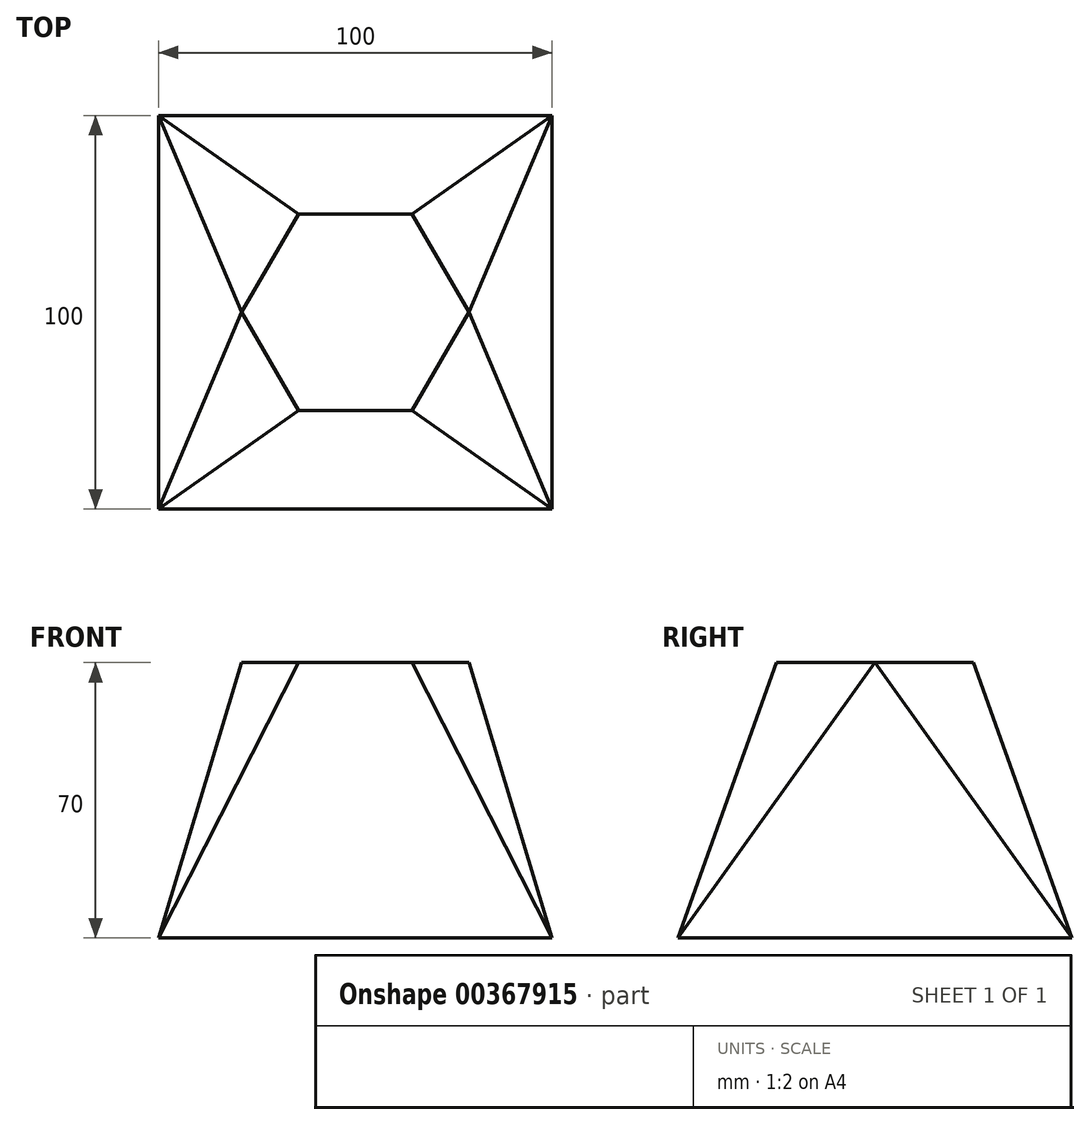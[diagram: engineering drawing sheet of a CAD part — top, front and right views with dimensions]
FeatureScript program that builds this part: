
annotation { "Feature Type Name" : "Feature", "Feature Type Description" : "" }
export const myFeature = defineFeature(function(context is Context, id is Id, definition is map)
    precondition{}
    {
        {
            var Q0;
            Q0=qCreatedBy(makeId("Top.planeOp"),FACE);
            cPlane(context, id + "F0", {"entities" : qUnion([Q0]), "cplaneType" : CPlaneType.OFFSET, "offset" : 70 * mm, "width" : 150 * mm, "height" : 150 * mm});
        }
        {
            var Q0;
            Q0=qCreatedBy(id+"F0.planeOp",FACE);
            var sketch = newSketch(context, id + "F1", { "sketchPlane" : qUnion([Q0])});
            skCircle(sketch, "E0.cCircle", {"center": v(0, 0) * mm, "radius": 25 * mm, "construction": true});
            skLineSegment(sketch, "E0.0", {"start": v(28.87, 0) * mm, "end": v(14.43, -25) * mm});
            skLineSegment(sketch, "E0.1", {"start": v(14.43, -25) * mm, "end": v(-14.43, -25) * mm});
            skLineSegment(sketch, "E0.2", {"start": v(-14.43, -25) * mm, "end": v(-28.87, 0) * mm});
            skLineSegment(sketch, "E0.3", {"start": v(-28.87, 0) * mm, "end": v(-14.43, 25) * mm});
            skLineSegment(sketch, "E0.4", {"start": v(-14.43, 25) * mm, "end": v(14.43, 25) * mm});
            skLineSegment(sketch, "E0.5", {"start": v(14.43, 25) * mm, "end": v(28.87, 0) * mm});
            skPoint(sketch, "E0.0.midPoint", {"position": v(21.65, -12.5) * mm});
            skLineSegment(sketch, "E1", {"start": v(-14.43, 25) * mm, "end": v(-14.43, -25) * mm});
            skLineSegment(sketch, "E2", {"start": v(14.43, 25) * mm, "end": v(14.43, -25) * mm});
            skSolve(sketch);
        }
        {
            var Q0;
            Q0=qCreatedBy(makeId("Top.planeOp"),FACE);
            var sketch = newSketch(context, id + "F2", { "sketchPlane" : qUnion([Q0])});
            skLineSegment(sketch, "E3.bottom", {"start": v(-50, 50) * mm, "end": v(50, 50) * mm});
            skLineSegment(sketch, "E3.top", {"start": v(-50, -50) * mm, "end": v(50, -50) * mm});
            skLineSegment(sketch, "E3.left", {"start": v(-50, 50) * mm, "end": v(-50, -50) * mm});
            skLineSegment(sketch, "E3.right", {"start": v(50, 50) * mm, "end": v(50, -50) * mm});
            skLineSegment(sketch, "E4", {"start": v(0, -50) * mm, "end": v(0, 50) * mm, "construction": true});
            skSolve(sketch);
        }
        {
            var Q0;
            Q0=makeQuery(id+"F1.imprint","IMPRINT",FACE,{"disambiguationData":[TD([[makeQuery(id+"F1.imprint","IMPRINT",EDGE,{"derivedFrom":sQuery(id+"F1.wireOp",EDGE,"E0.1")}),-1.0]])]});
            var Q1;
            Q1=makeQuery(id+"F2.imprint","IMPRINT",FACE,{"disambiguationData":[TD([[makeQuery(id+"F2.imprint","IMPRINT",EDGE,{"derivedFrom":sQuery(id+"F2.wireOp",EDGE,"E3.bottom")}),-1.0]])]});
            loft(context, id + "F3", {"sheetProfilesArray" : [{ "sheetProfileEntities" : qUnion([Q0]) }, { "sheetProfileEntities" : qUnion([Q1]) }]});
        }
        {
            var Q1;
            Q1=makeQuery(id+"F1.imprint","IMPRINT",FACE,{"disambiguationData":[TD([[makeQuery(id+"F1.imprint","IMPRINT",EDGE,{"derivedFrom":sQuery(id+"F1.wireOp",EDGE,"E0.2")}),-1.0]])]});
            var Q2;
            Q2=sQuery(id+"F2.wireOp",VERTEX,"E3.left.end");
            loft(context, id + "F4", {"operationType" : NewBodyOperationType.ADD, "sheetProfilesArray" : [{ "sheetProfileEntities" : qUnion([Q1]) }, { "sheetProfileEntities" : qUnion([Q2]) }]});
        }
        {
            var Q1;
            Q1=makeQuery(id+"F1.imprint","IMPRINT",FACE,{"disambiguationData":[TD([[makeQuery(id+"F1.imprint","IMPRINT",EDGE,{"derivedFrom":sQuery(id+"F1.wireOp",EDGE,"E0.2")}),-1.0]])]});
            var Q2;
            Q2=sQuery(id+"F2.wireOp",VERTEX,"E3.left.start");
            loft(context, id + "F5", {"operationType" : NewBodyOperationType.ADD, "sheetProfilesArray" : [{ "sheetProfileEntities" : qUnion([Q1]) }, { "sheetProfileEntities" : qUnion([Q2]) }]});
        }
        {
            var Q1;
            Q1=makeQuery(id+"F5.opLoft","SWEPT_FACE",FACE,{"disambiguationData":[OSD([sQuery(id+"F1.wireOp",EDGE,"E0.1"),sQuery(id+"F1.wireOp",EDGE,"E0.2"),sQuery(id+"F1.wireOp",EDGE,"E0.3"),sQuery(id+"F1.wireOp",EDGE,"E1")])]});
            var Q2;
            Q2=makeQuery(id+"F4.opLoft","SWEPT_FACE",FACE,{"disambiguationData":[OSD([sQuery(id+"F1.wireOp",EDGE,"E0.2"),sQuery(id+"F1.wireOp",EDGE,"E0.3"),sQuery(id+"F1.wireOp",EDGE,"E0.4"),sQuery(id+"F1.wireOp",EDGE,"E1")])]});
            var Q3;
            Q3=sQuery(id+"F2.wireOp",VERTEX,"E3.bottom.start");
            var Q4;
            Q4=sQuery(id+"F2.wireOp",VERTEX,"E3.left.end");
            loft(context, id + "F6", {"operationType" : NewBodyOperationType.ADD, "sheetProfilesArray" : [{ "sheetProfileEntities" : qUnion([Q1]) }, { "sheetProfileEntities" : qUnion([Q2]) }], "matchConnections" : true, "connections" : [{ "connectionEntities" : qUnion([Q3, Q4]), "connectionEdgeQueries" : qUnion([]), "connectionEdgeParameters" : [] }]});
        }
        {
            var Q1;
            Q1=makeQuery(id+"F1.imprint","IMPRINT",FACE,{"disambiguationData":[TD([[makeQuery(id+"F1.imprint","IMPRINT",EDGE,{"derivedFrom":sQuery(id+"F1.wireOp",EDGE,"E0.0")}),-1.0]])]});
            var Q2;
            Q2=sQuery(id+"F2.wireOp",VERTEX,"E3.right.start");
            loft(context, id + "F7", {"operationType" : NewBodyOperationType.ADD, "sheetProfilesArray" : [{ "sheetProfileEntities" : qUnion([Q1]) }, { "sheetProfileEntities" : qUnion([Q2]) }]});
        }
        {
            var Q1;
            Q1=makeQuery(id+"F1.imprint","IMPRINT",FACE,{"disambiguationData":[TD([[makeQuery(id+"F1.imprint","IMPRINT",EDGE,{"derivedFrom":sQuery(id+"F1.wireOp",EDGE,"E0.0")}),-1.0]])]});
            var Q2;
            Q2=sQuery(id+"F2.wireOp",VERTEX,"E3.right.end");
            loft(context, id + "F8", {"operationType" : NewBodyOperationType.ADD, "sheetProfilesArray" : [{ "sheetProfileEntities" : qUnion([Q1]) }, { "sheetProfileEntities" : qUnion([Q2]) }]});
        }
        {
            var Q1;
            Q1=makeQuery(id+"F8.opLoft","SWEPT_FACE",FACE,{"disambiguationData":[OSD([sQuery(id+"F1.wireOp",EDGE,"E0.0"),sQuery(id+"F1.wireOp",EDGE,"E0.4"),sQuery(id+"F1.wireOp",EDGE,"E0.5"),sQuery(id+"F1.wireOp",EDGE,"E2")])]});
            var Q2;
            Q2=makeQuery(id+"F7.opLoft","SWEPT_FACE",FACE,{"disambiguationData":[OSD([sQuery(id+"F1.wireOp",EDGE,"E0.0"),sQuery(id+"F1.wireOp",EDGE,"E0.1"),sQuery(id+"F1.wireOp",EDGE,"E0.5"),sQuery(id+"F1.wireOp",EDGE,"E2")])]});
            var Q3;
            Q3=sQuery(id+"F2.wireOp",VERTEX,"E3.right.end");
            var Q4;
            Q4=sQuery(id+"F2.wireOp",VERTEX,"E3.right.start");
            loft(context, id + "F9", {"operationType" : NewBodyOperationType.ADD, "sheetProfilesArray" : [{ "sheetProfileEntities" : qUnion([Q1]) }, { "sheetProfileEntities" : qUnion([Q2]) }], "matchConnections" : true, "connections" : [{ "connectionEntities" : qUnion([Q3, Q4]), "connectionEdgeQueries" : qUnion([]), "connectionEdgeParameters" : [] }]});
        }
    });
